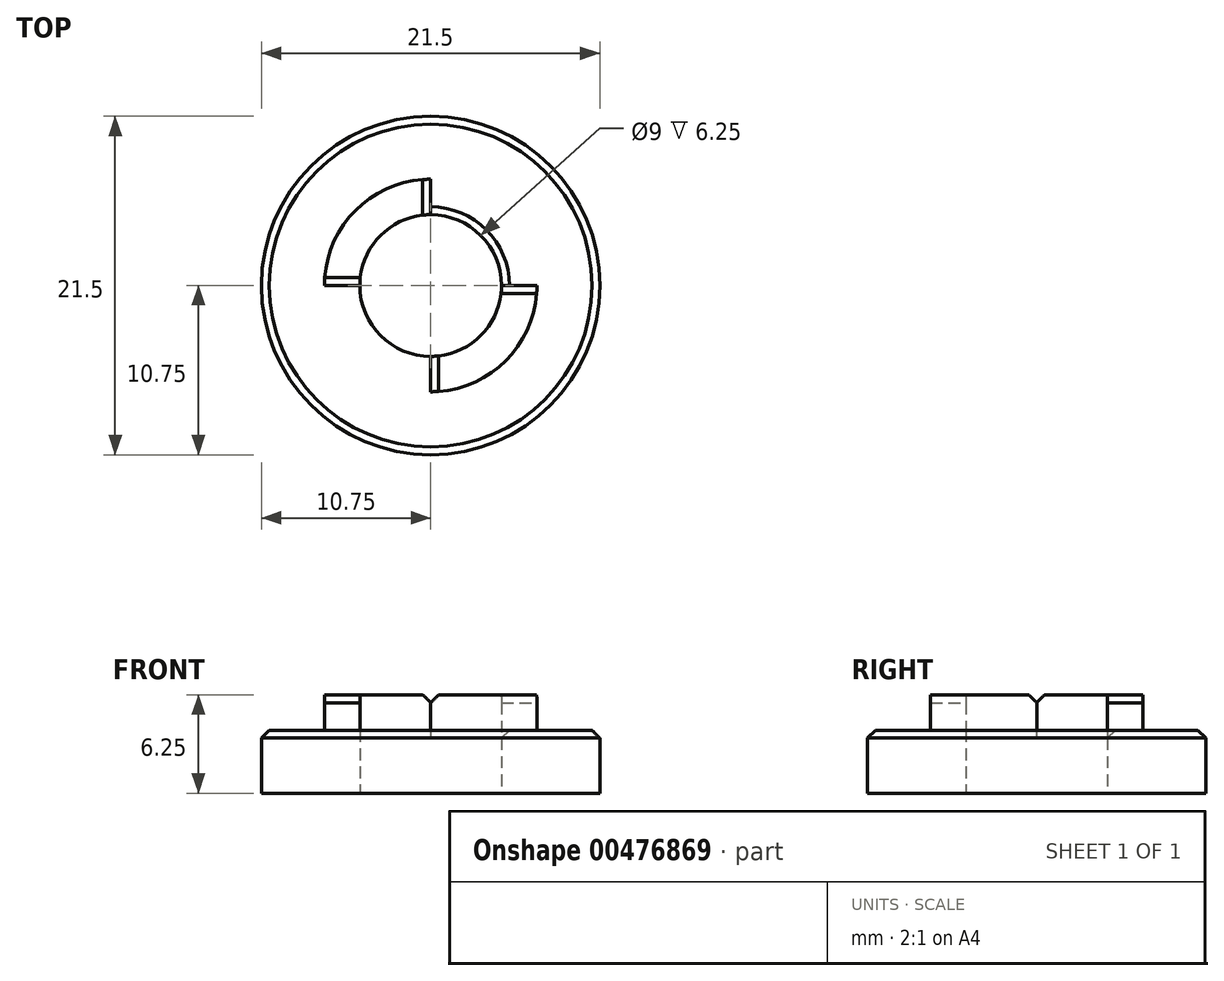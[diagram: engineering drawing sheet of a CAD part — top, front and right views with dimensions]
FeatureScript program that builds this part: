
annotation { "Feature Type Name" : "Feature", "Feature Type Description" : "" }
export const myFeature = defineFeature(function(context is Context, id is Id, definition is map)
    precondition{}
    {
        {
            var Q0;
            Q0=qCreatedBy(makeId("Top.planeOp"),FACE);
            var sketch = newSketch(context, id + "F0", { "sketchPlane" : qUnion([Q0])});
            skCircle(sketch, "E0", {"center": v(0, 0) * mm, "radius": 10.75 * mm});
            skCircle(sketch, "E1", {"center": v(0, 0) * mm, "radius": 4.5 * mm});
            skSolve(sketch);
        }
        {
            var Q0;
            Q0 = qSketchRegion(id + "F0", true);
            extrude(context, id + "F1", {"entities" : qUnion([Q0]), "depth" : 4 * mm});
        }
        {
            var Q0;
            Q0=qCreatedBy(makeId("Top.planeOp"),FACE);
            var sketch = newSketch(context, id + "F2", { "sketchPlane" : qUnion([Q0])});
            skCircle(sketch, "E2", {"center": v(0, 0) * mm, "radius": 4.5 * mm});
            skCircle(sketch, "E3", {"center": v(0, 0) * mm, "radius": 6.75 * mm});
            skSolve(sketch);
        }
        {
            var Q0;
            Q0 = qSketchRegion(id + "F2", true);
            extrude(context, id + "F3", {"entities" : qUnion([Q0]), "depth" : 6.25 * mm});
        }
        {
            var Q0;
            Q0=qCreatedBy(makeId("Top.planeOp"),FACE);
            var sketch = newSketch(context, id + "F4", { "sketchPlane" : qUnion([Q0])});
            skLineSegment(sketch, "E4", {"start": v(0, 0) * mm, "end": v(0, 12) * mm});
            skLineSegment(sketch, "E5", {"start": v(0, 12) * mm, "end": v(12, 12) * mm});
            skLineSegment(sketch, "E6", {"start": v(12, 12) * mm, "end": v(12, 0) * mm});
            skLineSegment(sketch, "E7", {"start": v(12, 0) * mm, "end": v(-12, 0) * mm});
            skLineSegment(sketch, "E8", {"start": v(-12, 0) * mm, "end": v(-12, -12) * mm});
            skLineSegment(sketch, "E9", {"start": v(-12, -12) * mm, "end": v(0, -12) * mm});
            skLineSegment(sketch, "E10", {"start": v(0, -12) * mm, "end": v(0, 0) * mm});
            skSolve(sketch);
        }
        {
            var Q0;
            Q0 = qSketchRegion(id + "F4", true);
            extrude(context, id + "F5", {"entities" : qUnion([Q0]), "depth" : 10 * mm});
        }
        {
            var Q0;
            Q0=makeQuery(id+"F5.opExtrude","SWEPT_BODY",BODY,{"disambiguationData":[OSD([sQuery(id+"F4.wireOp",EDGE,"E7"),sQuery(id+"F4.wireOp",EDGE,"E8"),sQuery(id+"F4.wireOp",EDGE,"E9"),sQuery(id+"F4.wireOp",EDGE,"E10")])]});
            var Q1;
            Q1=makeQuery(id+"F5.opExtrude","SWEPT_BODY",BODY,{"disambiguationData":[OSD([sQuery(id+"F4.wireOp",EDGE,"E4"),sQuery(id+"F4.wireOp",EDGE,"E5"),sQuery(id+"F4.wireOp",EDGE,"E6"),sQuery(id+"F4.wireOp",EDGE,"E7")])]});
            var Q2;
            Q2=makeQuery(id+"F3.opExtrude","SWEPT_BODY",BODY,{"disambiguationData":[OSD([sQuery(id+"F2.wireOp",EDGE,"E2"),sQuery(id+"F2.wireOp",EDGE,"E3")])]});
            booleanBodies(context, id + "F6", {"operationType" : BooleanOperationType.SUBTRACTION, "tools" : qUnion([Q0, Q1]), "targets" : qUnion([Q2])});
        }
        {
            var Q0;
            Q0=makeQuery(id+"F1.opExtrude","SWEPT_BODY",BODY,{"disambiguationData":[OSD([sQuery(id+"F0.wireOp",EDGE,"E0"),sQuery(id+"F0.wireOp",EDGE,"E1")])]});
            var Q1;
            Q1=makeQuery(id+"F6.opBoolean","SPLIT",BODY,{"disambiguationData":[OD(0.0)],"derivedFrom":makeQuery(id+"F3.opExtrude","SWEPT_BODY",BODY,{"disambiguationData":[OSD([sQuery(id+"F2.wireOp",EDGE,"E2"),sQuery(id+"F2.wireOp",EDGE,"E3")])]})});
            var Q2;
            Q2=makeQuery(id+"F6.opBoolean","SPLIT",BODY,{"disambiguationData":[OD(1.0)],"derivedFrom":makeQuery(id+"F3.opExtrude","SWEPT_BODY",BODY,{"disambiguationData":[OSD([sQuery(id+"F2.wireOp",EDGE,"E2"),sQuery(id+"F2.wireOp",EDGE,"E3")])]})});
            booleanBodies(context, id + "F7", {"operationType" : BooleanOperationType.UNION, "tools" : qUnion([Q0, Q1, Q2])});
        }
        {
            var Q0;
            {var subQ0=sQuery(id+"F4.wireOp",EDGE,"E7");Q0=makeQuery(id+"F6.opBoolean","INTERSECT",EDGE,{"derivedFrom":[makeQuery(id+"F3.opExtrude","CAP_FACE",FACE,{"disambiguationData":[OSD([sQuery(id+"F2.wireOp",EDGE,"E2"),sQuery(id+"F2.wireOp",EDGE,"E3")])],"isStart":false}),makeQuery(id+"F5.opExtrude","SWEPT_FACE",FACE,{"disambiguationData":[OSD([subQ0]),TDD([makeQuery(id+"F4.imprint","IMPRINT",EDGE,{"disambiguationData":[TD([[makeQuery(id+"F4.imprint","INTERSECT",VERTEX,{"derivedFrom":[subQ0,sQuery(id+"F4.wireOp",EDGE,"E8")]}),1.0]])],"derivedFrom":subQ0})])]})]});}
            var Q1;
            Q1=makeQuery(id+"F6.opBoolean","INTERSECT",EDGE,{"derivedFrom":[makeQuery(id+"F3.opExtrude","CAP_FACE",FACE,{"disambiguationData":[OSD([sQuery(id+"F2.wireOp",EDGE,"E2"),sQuery(id+"F2.wireOp",EDGE,"E3")])],"isStart":false}),makeQuery(id+"F5.opExtrude","SWEPT_FACE",FACE,{"disambiguationData":[OSD([sQuery(id+"F4.wireOp",EDGE,"E4")])]})]});
            var Q2;
            Q2=makeQuery(id+"F6.opBoolean","INTERSECT",EDGE,{"derivedFrom":[makeQuery(id+"F3.opExtrude","CAP_FACE",FACE,{"disambiguationData":[OSD([sQuery(id+"F2.wireOp",EDGE,"E2"),sQuery(id+"F2.wireOp",EDGE,"E3")])],"isStart":false}),makeQuery(id+"F5.opExtrude","SWEPT_FACE",FACE,{"disambiguationData":[OSD([sQuery(id+"F4.wireOp",EDGE,"E10")])]})]});
            var Q3;
            {var subQ0=sQuery(id+"F4.wireOp",EDGE,"E7");Q3=makeQuery(id+"F6.opBoolean","INTERSECT",EDGE,{"derivedFrom":[makeQuery(id+"F3.opExtrude","CAP_FACE",FACE,{"disambiguationData":[OSD([sQuery(id+"F2.wireOp",EDGE,"E2"),sQuery(id+"F2.wireOp",EDGE,"E3")])],"isStart":false}),makeQuery(id+"F5.opExtrude","SWEPT_FACE",FACE,{"disambiguationData":[OSD([subQ0]),TDD([makeQuery(id+"F4.imprint","IMPRINT",EDGE,{"disambiguationData":[TD([[makeQuery(id+"F4.imprint","INTERSECT",VERTEX,{"derivedFrom":[sQuery(id+"F4.wireOp",EDGE,"E6"),subQ0]}),-1.0]])],"derivedFrom":subQ0})])]})]});}
            var Q4;
            Q4=makeQuery(id+"F1.opExtrude","CAP_EDGE",EDGE,{"disambiguationData":[OSD([sQuery(id+"F0.wireOp",EDGE,"E0")])],"isStart":false});
            var Q5;
            {var subQ0=sQuery(id+"F0.wireOp",EDGE,"E1");var subQ1=sQuery(id+"F4.wireOp",EDGE,"E4");Q5=makeQuery(id+"F7.opBoolean","SPLIT",EDGE,{"disambiguationData":[TD([makeQuery(id+"F6.opBoolean","COPY",FACE,{"derivedFrom":makeQuery(id+"F5.opExtrude","SWEPT_FACE",FACE,{"disambiguationData":[OSD([subQ1])]})})])],"derivedFrom":makeQuery(id+"F1.opExtrude","CAP_EDGE",EDGE,{"disambiguationData":[OSD([subQ0])],"isStart":false})});}
            chamfer(context, id + "F8", {"entities" : qUnion([Q0, Q1, Q2, Q3, Q4, Q5]), "width" : 0.5 * mm, "tangentPropagation" : true});
        }
    });
